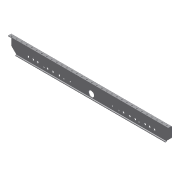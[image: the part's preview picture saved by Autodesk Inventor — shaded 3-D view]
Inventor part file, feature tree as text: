
AUTODESK INVENTOR PART (.ipt)
format: ipt  version: 2013 (Build 170138000, 138)  size: 169,472 bytes
history: native  units: in
note: dims shown in document units (in); Inventor stores cm internally (conversion verified against a paired STEP export)
features: mirror x1, other x1, imported_body x1
ambient origin geometry x8: Origin, YZ Plane, XZ Plane, XY Plane, X Axis, Y Axis, Z Axis, Center Point
feature tree (3):
  mirror  "Mirror1"
  other  "am-2572 Outer Plate1"
  imported_body  "Base1"
